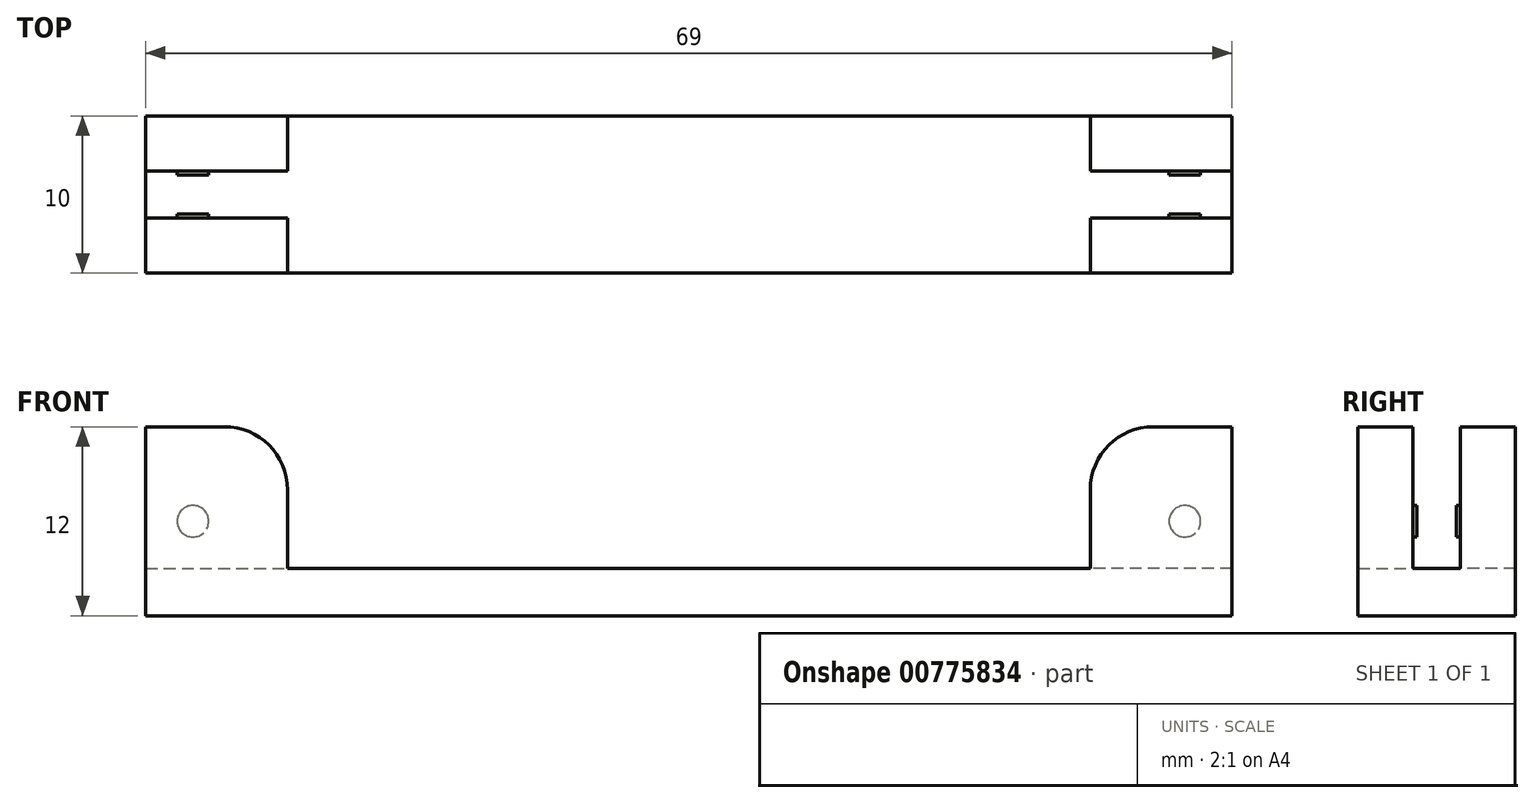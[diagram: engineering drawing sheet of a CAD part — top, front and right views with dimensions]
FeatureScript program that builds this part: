
annotation { "Feature Type Name" : "Feature", "Feature Type Description" : "" }
export const myFeature = defineFeature(function(context is Context, id is Id, definition is map)
    precondition{}
    {
        {
            assignVariable(context, id + "F0", {"name" : "speakerpostw", "anyValue" : 9 * mm});
        }
        {
            assignVariable(context, id + "F1", {"name" : "thick", "anyValue" : 3 * mm});
        }
        {
            var Q0;
            Q0=qCreatedBy(makeId("Top.planeOp"),FACE);
            var sketch = newSketch(context, id + "F2", { "sketchPlane" : qUnion([Q0])});
            skLineSegment(sketch, "E0.bottom", {"start": v(34.5, -5) * mm, "end": v(-34.5, -5) * mm});
            skLineSegment(sketch, "E0.top", {"start": v(34.5, 5) * mm, "end": v(-34.5, 5) * mm});
            skLineSegment(sketch, "E0.left", {"start": v(34.5, -5) * mm, "end": v(34.5, 5) * mm});
            skLineSegment(sketch, "E0.right", {"start": v(-34.5, -5) * mm, "end": v(-34.5, 5) * mm});
            skPoint(sketch, "E0.middle", {"position": v(0, 0) * mm});
            skSolve(sketch);
        }
        {
            var Q0;
            Q0=makeQuery(id+"F2.imprint","IMPRINT",FACE,{"disambiguationData":[TD([[makeQuery(id+"F2.imprint","IMPRINT",EDGE,{"derivedFrom":sQuery(id+"F2.wireOp",EDGE,"E0.bottom")}),-1.0]])]});
            extrude(context, id + "F3", {"entities" : qUnion([Q0]), "depth" : getVariable(context, 'thick'), "offsetDistance" : 25 * mm});
        }
        {
            var Q0;
            Q0=makeQuery(id+"F3.opExtrude","CAP_FACE",FACE,{"disambiguationData":[OSD([sQuery(id+"F2.wireOp",EDGE,"E0.bottom"),sQuery(id+"F2.wireOp",EDGE,"E0.top"),sQuery(id+"F2.wireOp",EDGE,"E0.left"),sQuery(id+"F2.wireOp",EDGE,"E0.right")])],"isStart":false});
            var sketch = newSketch(context, id + "F4", { "sketchPlane" : qUnion([Q0])});
            skLineSegment(sketch, "E1.bottom", {"start": v(-34.5, 5) * mm, "end": v(-25.5, 5) * mm});
            skLineSegment(sketch, "E1.top", {"start": v(-34.5, 1.5) * mm, "end": v(-25.5, 1.5) * mm});
            skLineSegment(sketch, "E1.left", {"start": v(-34.5, 5) * mm, "end": v(-34.5, 1.5) * mm});
            skLineSegment(sketch, "E1.right", {"start": v(-25.5, 5) * mm, "end": v(-25.5, 1.5) * mm});
            skSolve(sketch);
        }
        {
            var Q0;
            Q0=makeQuery(id+"F4.imprint","IMPRINT",FACE,{"disambiguationData":[TD([[makeQuery(id+"F4.imprint","IMPRINT",EDGE,{"derivedFrom":sQuery(id+"F4.wireOp",EDGE,"E1.bottom")}),1.0]])]});
            extrude(context, id + "F5", {"entities" : qUnion([Q0]), "operationType" : NewBodyOperationType.ADD, "depth" : getVariable(context, 'speakerpostw'), "offsetDistance" : 25 * mm});
        }
        {
            var Q0;
            Q0=makeQuery(id+"F5.opExtrude","SWEPT_FACE",FACE,{"disambiguationData":[OSD([sQuery(id+"F4.wireOp",EDGE,"E1.top")])]});
            var sketch = newSketch(context, id + "F6", { "sketchPlane" : qUnion([Q0])});
            skLineSegment(sketch, "E2.bottom", {"start": v(-34.5, 3) * mm, "end": v(-31.5, 3) * mm});
            skLineSegment(sketch, "E2.top", {"start": v(-34.5, 6) * mm, "end": v(-31.5, 6) * mm, "construction": true});
            skLineSegment(sketch, "E2.left", {"start": v(-34.5, 3) * mm, "end": v(-34.5, 6) * mm});
            skLineSegment(sketch, "E2.right", {"start": v(-31.5, 3) * mm, "end": v(-31.5, 6) * mm, "construction": true});
            skCircle(sketch, "E3", {"center": v(-31.5, 6) * mm, "radius": 1 * mm});
            skSolve(sketch);
        }
        {
            var Q0;
            Q0=makeQuery(id+"F6.imprint","IMPRINT",FACE,{"disambiguationData":[TD([[makeQuery(id+"F6.imprint","IMPRINT",EDGE,{"derivedFrom":sQuery(id+"F6.wireOp",EDGE,"E3")}),1.0]])]});
            var Q1;
            Q1=sQuery(id+"F6.wireOp",EDGE,"E3");
            extrude(context, id + "F7", {"entities" : qUnion([Q0]), "operationType" : NewBodyOperationType.ADD, "surfaceOperationType" : NewSurfaceOperationType.ADD, "surfaceEntities" : qUnion([Q1]), "depth" : .25 * mm, "offsetDistance" : 25 * mm});
        }
        {
            var Q0;
            Q0=makeQuery(id+"F5.opExtrude","CAP_EDGE",EDGE,{"disambiguationData":[OSD([sQuery(id+"F4.wireOp",EDGE,"E1.right")])],"isStart":false});
            fillet(context, id + "F8", {"entities" : qUnion([Q0]), "radius" : 4 * mm, "tangentPropagation" : true, "allowEdgeOverflow" : false});
        }
        {
            var Q0;
            Q0=makeQuery(id+"F3.opExtrude","SWEPT_BODY",BODY,{"disambiguationData":[OSD([sQuery(id+"F2.wireOp",EDGE,"E0.bottom"),sQuery(id+"F2.wireOp",EDGE,"E0.top"),sQuery(id+"F2.wireOp",EDGE,"E0.left"),sQuery(id+"F2.wireOp",EDGE,"E0.right")])]});
            var Q1;
            Q1=qCreatedBy(makeId("Right.planeOp"),FACE);
            mirror(context, id + "F9", {"operationType" : NewBodyOperationType.ADD, "entities" : qUnion([Q0]), "mirrorPlane" : qUnion([Q1])});
        }
        {
            var Q0;
            Q0=makeQuery(id+"F3.opExtrude","SWEPT_BODY",BODY,{"disambiguationData":[OSD([sQuery(id+"F2.wireOp",EDGE,"E0.bottom"),sQuery(id+"F2.wireOp",EDGE,"E0.top"),sQuery(id+"F2.wireOp",EDGE,"E0.left"),sQuery(id+"F2.wireOp",EDGE,"E0.right")])]});
            var Q1;
            Q1=qCreatedBy(makeId("Front.planeOp"),FACE);
            mirror(context, id + "F10", {"operationType" : NewBodyOperationType.ADD, "entities" : qUnion([Q0]), "mirrorPlane" : qUnion([Q1])});
        }
    });
